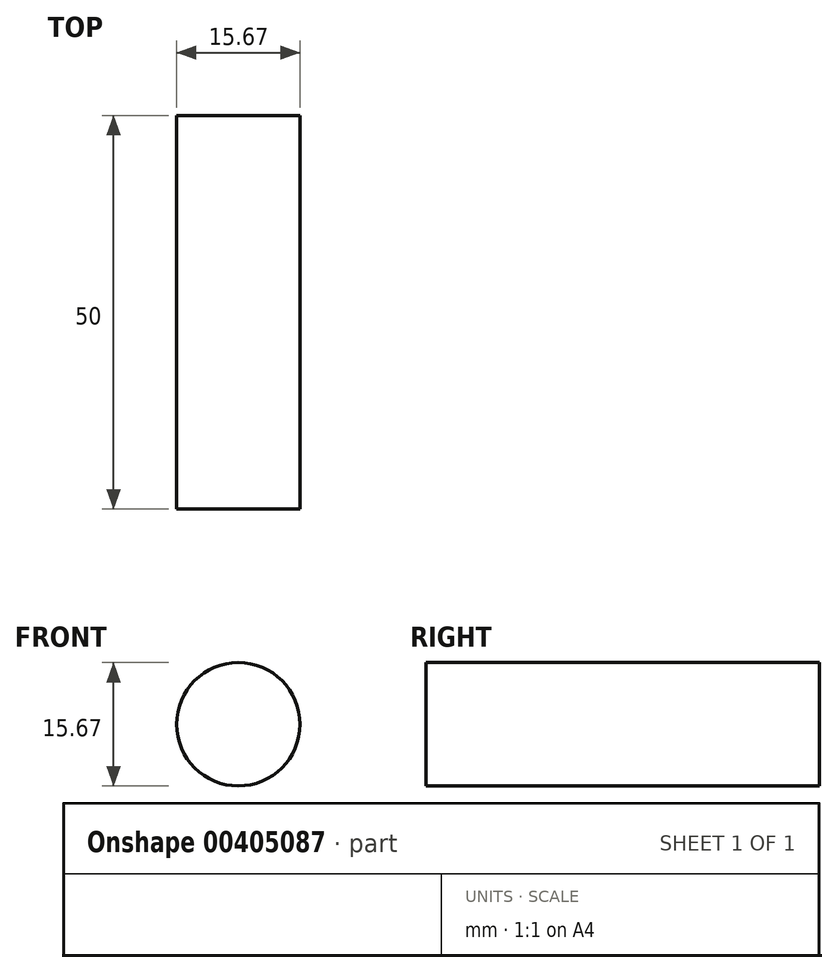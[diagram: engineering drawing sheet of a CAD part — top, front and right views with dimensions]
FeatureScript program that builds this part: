
annotation { "Feature Type Name" : "Feature", "Feature Type Description" : "" }
export const myFeature = defineFeature(function(context is Context, id is Id, definition is map)
    precondition{}
    {
        {
            var Q0;
            Q0=qCreatedBy(makeId("Front.planeOp"),FACE);
            var sketch = newSketch(context, id + "F0", { "sketchPlane" : qUnion([Q0])});
            skCircle(sketch, "E0", {"center": v(-55.9, 48.74) * mm, "radius": 15.52 * mm});
            skCircle(sketch, "E1", {"center": v(-55.9, 48.74) * mm, "radius": 7.84 * mm});
            skSolve(sketch);
        }
        {
            var Q0;
            Q0=makeQuery(id+"F0.imprint","IMPRINT",FACE,{"disambiguationData":[TD([[makeQuery(id+"F0.imprint","IMPRINT",EDGE,{"derivedFrom":sQuery(id+"F0.wireOp",EDGE,"E1")}),1.0]])]});
            extrude(context, id + "F1", {"entities" : qUnion([Q0]), "depth" : 50 * mm});
        }
        {
            var Q0;
            Q0=sQuery(id+"F0.wireOp",EDGE,"E0");
            extrude(context, id + "F2", {"bodyType" : ToolBodyType.SURFACE, "surfaceEntities" : qUnion([Q0]), "depth" : 25 * mm, "hasSecondDirection" : true, "secondDirectionOppositeDirection" : false, "secondDirectionDepth" : 5 * mm});
        }
    });
